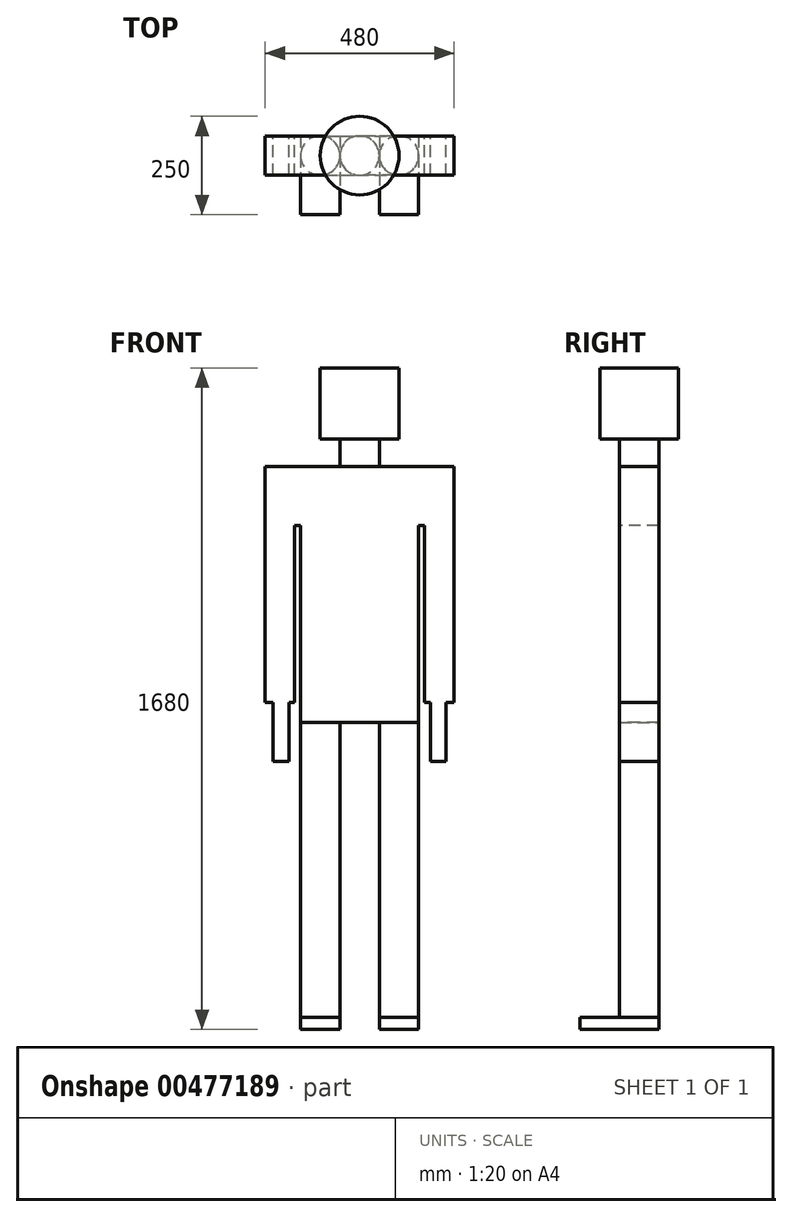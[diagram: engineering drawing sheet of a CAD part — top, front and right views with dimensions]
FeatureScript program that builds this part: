
annotation { "Feature Type Name" : "Feature", "Feature Type Description" : "" }
export const myFeature = defineFeature(function(context is Context, id is Id, definition is map)
    precondition{}
    {
        {
            var Q0;
            Q0=qCreatedBy(makeId("Top.planeOp"),FACE);
            var sketch = newSketch(context, id + "F0", { "sketchPlane" : qUnion([Q0])});
            skLineSegment(sketch, "E0.bottom", {"start": v(-150, 0) * mm, "end": v(-50, 0) * mm});
            skLineSegment(sketch, "E0.top", {"start": v(-150, -200) * mm, "end": v(-50, -200) * mm});
            skLineSegment(sketch, "E0.left", {"start": v(-150, 0) * mm, "end": v(-150, -200) * mm});
            skLineSegment(sketch, "E0.right", {"start": v(-50, 0) * mm, "end": v(-50, -200) * mm});
            skSolve(sketch);
        }
        {
            var Q0;
            Q0 = qSketchRegion(id + "F0", true);
            extrude(context, id + "F1", {"entities" : qUnion([Q0]), "depth" : 30 * mm});
        }
        {
            var Q0;
            Q0=makeQuery(id+"F1.opExtrude","CAP_FACE",FACE,{"disambiguationData":[OSD([sQuery(id+"F0.wireOp",EDGE,"E0.bottom"),sQuery(id+"F0.wireOp",EDGE,"E0.top"),sQuery(id+"F0.wireOp",EDGE,"E0.left"),sQuery(id+"F0.wireOp",EDGE,"E0.right")])],"isStart":false});
            var sketch = newSketch(context, id + "F2", { "sketchPlane" : qUnion([Q0])});
            skCircle(sketch, "E1", {"center": v(-100, -50) * mm, "radius": 50 * mm});
            skPoint(sketch, "E1.centerSnap0", {"position": v(-100, 0) * mm});
            skSolve(sketch);
        }
        {
            var Q0;
            Q0 = qSketchRegion(id + "F2", true);
            extrude(context, id + "F3", {"entities" : qUnion([Q0]), "operationType" : NewBodyOperationType.ADD, "depth" : 750 * mm});
        }
        {
            var Q0;
            Q0=makeQuery(id+"F3.opExtrude","CAP_FACE",FACE,{"disambiguationData":[OSD([sQuery(id+"F2.wireOp",EDGE,"E1")])],"isStart":false});
            var sketch = newSketch(context, id + "F4", { "sketchPlane" : qUnion([Q0])});
            skLineSegment(sketch, "E2.bottom", {"start": v(-150, 0) * mm, "end": v(0, 0) * mm});
            skLineSegment(sketch, "E2.top", {"start": v(-150, -100) * mm, "end": v(0, -100) * mm});
            skLineSegment(sketch, "E2.left", {"start": v(-150, 0) * mm, "end": v(-150, -100) * mm});
            skLineSegment(sketch, "E2.right", {"start": v(0, 0) * mm, "end": v(0, -100) * mm});
            skSolve(sketch);
        }
        {
            var Q0;
            Q0 = qSketchRegion(id + "F4", true);
            extrude(context, id + "F5", {"entities" : qUnion([Q0]), "operationType" : NewBodyOperationType.ADD, "depth" : 650 * mm});
        }
        {
            var Q0;
            Q0=makeQuery(id+"F5.opExtrude","CAP_FACE",FACE,{"disambiguationData":[OSD([sQuery(id+"F4.wireOp",EDGE,"E2.bottom"),sQuery(id+"F4.wireOp",EDGE,"E2.top"),sQuery(id+"F4.wireOp",EDGE,"E2.left"),sQuery(id+"F4.wireOp",EDGE,"E2.right")])],"isStart":false});
            var sketch = newSketch(context, id + "F6", { "sketchPlane" : qUnion([Q0])});
            skCircle(sketch, "E3", {"center": v(0, -50) * mm, "radius": 50 * mm});
            skSolve(sketch);
        }
        {
            var Q0;
            Q0 = qSketchRegion(id + "F6", true);
            extrude(context, id + "F7", {"entities" : qUnion([Q0]), "operationType" : NewBodyOperationType.ADD, "depth" : 250 * mm});
        }
        {
            var Q0;
            Q0=makeQuery(id+"F5.opExtrude","CAP_FACE",FACE,{"disambiguationData":[OSD([sQuery(id+"F4.wireOp",EDGE,"E2.bottom"),sQuery(id+"F4.wireOp",EDGE,"E2.top"),sQuery(id+"F4.wireOp",EDGE,"E2.left"),sQuery(id+"F4.wireOp",EDGE,"E2.right")])],"isStart":false});
            var sketch = newSketch(context, id + "F8", { "sketchPlane" : qUnion([Q0])});
            skLineSegment(sketch, "E4.bottom", {"start": v(0, 0) * mm, "end": v(-240, 0) * mm});
            skLineSegment(sketch, "E4.top", {"start": v(0, -100) * mm, "end": v(-240, -100) * mm});
            skLineSegment(sketch, "E4.left", {"start": v(0, 0) * mm, "end": v(0, -100) * mm});
            skLineSegment(sketch, "E4.right", {"start": v(-240, 0) * mm, "end": v(-240, -100) * mm});
            skSolve(sketch);
        }
        {
            var Q0;
            Q0 = qSketchRegion(id + "F8", true);
            extrude(context, id + "F9", {"entities" : qUnion([Q0]), "operationType" : NewBodyOperationType.ADD, "oppositeDirection" : true, "depth" : 150 * mm});
        }
        {
            var Q0;
            Q0=makeQuery(id+"F9.opExtrude","CAP_FACE",FACE,{"disambiguationData":[OSD([sQuery(id+"F8.wireOp",EDGE,"E4.bottom"),sQuery(id+"F8.wireOp",EDGE,"E4.top"),sQuery(id+"F8.wireOp",EDGE,"E4.left"),sQuery(id+"F8.wireOp",EDGE,"E4.right")])],"isStart":false});
            var sketch = newSketch(context, id + "F10", { "sketchPlane" : qUnion([Q0])});
            skLineSegment(sketch, "E5.bottom", {"start": v(-240, 100) * mm, "end": v(-165, 100) * mm});
            skLineSegment(sketch, "E5.top", {"start": v(-240, 0) * mm, "end": v(-165, 0) * mm});
            skLineSegment(sketch, "E5.left", {"start": v(-240, 100) * mm, "end": v(-240, 0) * mm});
            skLineSegment(sketch, "E5.right", {"start": v(-165, 100) * mm, "end": v(-165, 0) * mm});
            skSolve(sketch);
        }
        {
            var Q0;
            Q0 = qSketchRegion(id + "F10", true);
            extrude(context, id + "F11", {"entities" : qUnion([Q0]), "operationType" : NewBodyOperationType.ADD, "depth" : 450 * mm});
        }
        {
            var Q0;
            Q0=makeQuery(id+"F11.opExtrude","CAP_FACE",FACE,{"disambiguationData":[OSD([sQuery(id+"F10.wireOp",EDGE,"E5.bottom"),sQuery(id+"F10.wireOp",EDGE,"E5.top"),sQuery(id+"F10.wireOp",EDGE,"E5.left"),sQuery(id+"F10.wireOp",EDGE,"E5.right")])],"isStart":false});
            var sketch = newSketch(context, id + "F12", { "sketchPlane" : qUnion([Q0])});
            skLineSegment(sketch, "E6.bottom", {"start": v(-219.37, 100) * mm, "end": v(-179.5, 100) * mm});
            skLineSegment(sketch, "E6.top", {"start": v(-219.37, 0) * mm, "end": v(-179.5, 0) * mm});
            skLineSegment(sketch, "E6.left", {"start": v(-219.37, 100) * mm, "end": v(-219.37, 0) * mm});
            skLineSegment(sketch, "E6.right", {"start": v(-179.5, 100) * mm, "end": v(-179.5, 0) * mm});
            skSolve(sketch);
        }
        {
            var Q0;
            Q0 = qSketchRegion(id + "F12", true);
            extrude(context, id + "F13", {"entities" : qUnion([Q0]), "operationType" : NewBodyOperationType.ADD, "depth" : 150 * mm});
        }
        {
            var Q0;
            Q0=makeQuery(id+"F1.opExtrude","SWEPT_BODY",BODY,{"disambiguationData":[OSD([sQuery(id+"F0.wireOp",EDGE,"E0.bottom"),sQuery(id+"F0.wireOp",EDGE,"E0.top"),sQuery(id+"F0.wireOp",EDGE,"E0.left"),sQuery(id+"F0.wireOp",EDGE,"E0.right")])]});
            var Q1;
            Q1=qCreatedBy(makeId("Right.planeOp"),FACE);
            mirror(context, id + "F14", {"operationType" : NewBodyOperationType.ADD, "entities" : qUnion([Q0]), "mirrorPlane" : qUnion([Q1])});
        }
        {
            var Q0;
            Q0=makeQuery(id+"F7.opExtrude","CAP_FACE",FACE,{"disambiguationData":[OSD([sQuery(id+"F6.wireOp",EDGE,"E3")])],"isStart":false});
            var sketch = newSketch(context, id + "F15", { "sketchPlane" : qUnion([Q0])});
            skCircle(sketch, "E7", {"center": v(0, -50) * mm, "radius": 100 * mm});
            skSolve(sketch);
        }
        {
            var Q0;
            Q0 = qSketchRegion(id + "F15", true);
            extrude(context, id + "F16", {"entities" : qUnion([Q0]), "operationType" : NewBodyOperationType.ADD, "oppositeDirection" : true, "depth" : 180 * mm});
        }
    });
